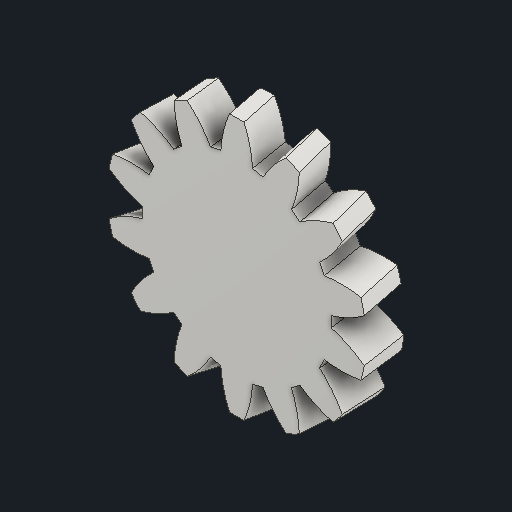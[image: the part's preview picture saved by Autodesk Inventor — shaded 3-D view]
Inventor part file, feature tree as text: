
AUTODESK INVENTOR PART (.ipt)
format: ipt  version: 2024.2 (Build 282272000, 272)  size: 352,768 bytes
history: native  units: in
note: dims shown in document units (in); Inventor stores cm internally (conversion verified against a paired STEP export)
features: other x12, plane x3, sketch x2
ambient origin geometry x8: Origin, YZ Plane, XZ Plane, XY Plane, X Axis, Y Axis, Z Axis, Center Point
bodies: Solid1 (feature_tree)
feature tree (17):
  other  "Spur Gear2"
  other  "Solid1::Spur Gear2"
  other  "TaggingFeature1"
  sketch  "Sketch1"  dims[d0=0.3937in]
  sketch  "Sketch2"  dims[d9=0.0in d14=0.0in d15=1.3982in d16=0.0in d17=0.0in d18=0.0in d19=1.3982in]
  plane  "XZ Plane_1"
  plane  "Work Plane2"
  plane  "Work Plane3"
  other  "Srf1"
  other  "Srf1::Derived"
  other  "Start plane iMate"
  other  "Distance iMate"
  other  "Position iMate"
  other  "Mesh iMate"
  other  "Axis iMate"
  other  "Mesh iMate2"
  other  "Align iMate"
